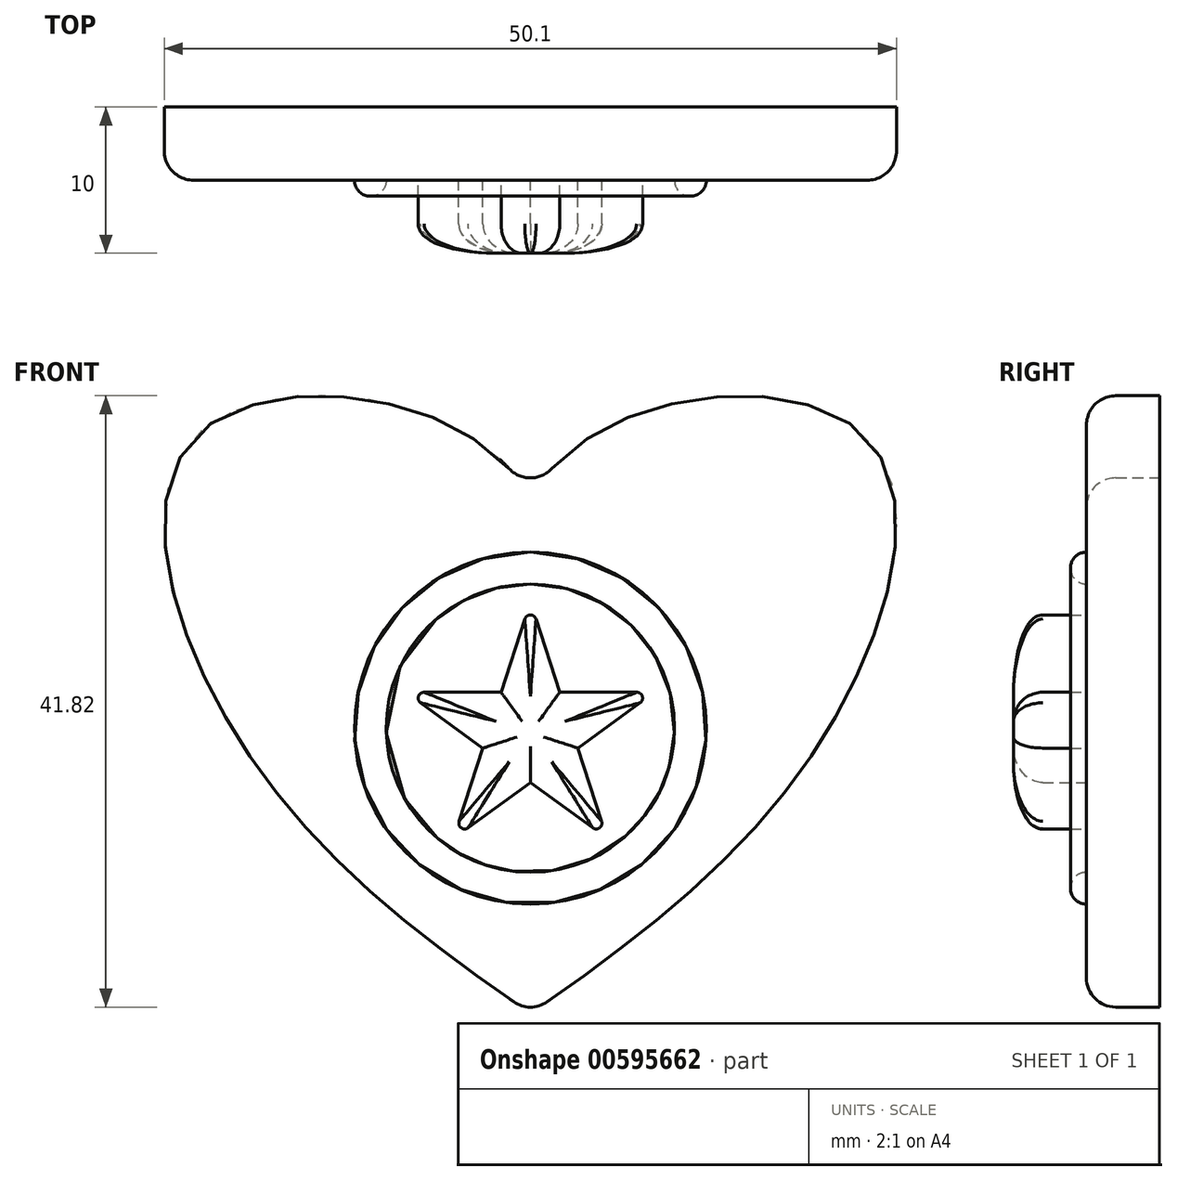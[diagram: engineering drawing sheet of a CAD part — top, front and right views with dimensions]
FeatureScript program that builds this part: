
annotation { "Feature Type Name" : "Feature", "Feature Type Description" : "" }
export const myFeature = defineFeature(function(context is Context, id is Id, definition is map)
    precondition{}
    {
        {
            var Q0;
            Q0=qCreatedBy(makeId("Front.planeOp"),FACE);
            var sketch = newSketch(context, id + "F0", { "sketchPlane" : qUnion([Q0])});
            skFitSpline(sketch, "E0", {"points": [v(0, 4.74) * mm, v(-22.34, 9.53) * mm, v(-20.92, -10.1) * mm, v(0, -30.47) * mm], "startDerivative": vector(-35.89, 67.68) * mm, "endDerivative": vector(70.46, -48.53) * mm});
            skFitSpline(sketch, "E1.MirrorCS", {"points": [v(0, 4.74) * mm, v(22.34, 9.53) * mm, v(20.92, -10.1) * mm, v(0, -30.47) * mm], "startDerivative": vector(35.89, 67.68) * mm, "endDerivative": vector(-70.46, -48.53) * mm});
            skPoint(sketch, "E2", {"position": v(-25, 1.75) * mm});
            skPoint(sketch, "E3", {"position": v(25, 1.75) * mm});
            skSolve(sketch);
        }
        {
            var Q0;
            Q0=makeQuery(id+"F0.imprint","IMPRINT",FACE,{"disambiguationData":[TD([[makeQuery(id+"F0.imprint","IMPRINT",EDGE,{"derivedFrom":sQuery(id+"F0.wireOp",EDGE,"E0")}),1.0]])]});
            extrude(context, id + "F1", {"entities" : qUnion([Q0]), "depth" : 5 * mm, "offsetDistance" : 25 * mm});
        }
        {
            var Q0;
            Q0=makeQuery(id+"F1.opExtrude","CAP_FACE",FACE,{"disambiguationData":[OSD([sQuery(id+"F0.wireOp",EDGE,"E0"),sQuery(id+"F0.wireOp",EDGE,"E1.MirrorCS")])],"isStart":false});
            var sketch = newSketch(context, id + "F2", { "sketchPlane" : qUnion([Q0])});
            skLineSegment(sketch, "E4", {"start": v(-0.38, -3.48) * mm, "end": v(-2, -8.5) * mm});
            skLineSegment(sketch, "E5", {"start": v(-2, -8.5) * mm, "end": v(-7.28, -8.5) * mm});
            skLineSegment(sketch, "E6", {"start": v(-7.51, -9.21) * mm, "end": v(-3.25, -12.31) * mm});
            skLineSegment(sketch, "E7", {"start": v(-3.25, -12.31) * mm, "end": v(-4.88, -17.32) * mm});
            skLineSegment(sketch, "E8", {"start": v(-4.26, -17.77) * mm, "end": v(0, -14.67) * mm});
            skLineSegment(sketch, "E9.MirrorCS", {"start": v(0.38, -3.48) * mm, "end": v(2, -8.5) * mm});
            skLineSegment(sketch, "E10.MirrorCS", {"start": v(2, -8.5) * mm, "end": v(7.28, -8.5) * mm});
            skLineSegment(sketch, "E11.MirrorCS", {"start": v(7.51, -9.21) * mm, "end": v(3.25, -12.31) * mm});
            skLineSegment(sketch, "E12.MirrorCS", {"start": v(3.25, -12.31) * mm, "end": v(4.88, -17.32) * mm});
            skLineSegment(sketch, "E13.MirrorCS", {"start": v(4.26, -17.77) * mm, "end": v(0, -14.67) * mm});
            skPoint(sketch, "E14.visualSharp", {"position": v(5.26, -18.5) * mm});
            skArc(sketch, "E14.filletArc", {"start": v(4.26, -17.77) * mm, "mid": v(4.73, -17.77) * mm, "end": v(4.88, -17.32) * mm});
            skPoint(sketch, "E15.visualSharp", {"position": v(8.5, -8.5) * mm});
            skArc(sketch, "E15.filletArc", {"start": v(7.51, -9.21) * mm, "mid": v(7.66, -8.77) * mm, "end": v(7.28, -8.5) * mm});
            skPoint(sketch, "E16.visualSharp", {"position": v(0, -2.3) * mm});
            skArc(sketch, "E16.filletArc", {"start": v(0.38, -3.48) * mm, "mid": v(0, -3.2) * mm, "end": v(-0.38, -3.48) * mm});
            skPoint(sketch, "E17.visualSharp", {"position": v(-8.5, -8.5) * mm});
            skArc(sketch, "E17.filletArc", {"start": v(-7.28, -8.5) * mm, "mid": v(-7.66, -8.77) * mm, "end": v(-7.51, -9.21) * mm});
            skPoint(sketch, "E18.visualSharp", {"position": v(-5.26, -18.5) * mm});
            skArc(sketch, "E18.filletArc", {"start": v(-4.88, -17.32) * mm, "mid": v(-4.73, -17.77) * mm, "end": v(-4.26, -17.77) * mm});
            skSolve(sketch);
        }
        {
            var Q0;
            Q0=makeQuery(id+"F2.imprint","IMPRINT",FACE,{"disambiguationData":[TD([[makeQuery(id+"F2.imprint","IMPRINT",EDGE,{"derivedFrom":sQuery(id+"F2.wireOp",EDGE,"E4")}),1.0]])]});
            extrude(context, id + "F3", {"entities" : qUnion([Q0]), "operationType" : NewBodyOperationType.ADD, "depth" : 5 * mm, "offsetDistance" : 25 * mm});
        }
        {
            var Q0;
            Q0=qCreatedBy(makeId("Right.planeOp"),FACE);
            var sketch = newSketch(context, id + "F4", { "sketchPlane" : qUnion([Q0])});
            skArc(sketch, "E19", {"start": v(-5, 1.09) * mm, "mid": v(-6.1, 0) * mm, "end": v(-5, -1.09) * mm});
            skLineSegment(sketch, "E20", {"start": v(-5, 1.09) * mm, "end": v(-5, -1.09) * mm});
            skSolve(sketch);
        }
        {
            var Q0;
            Q0=makeQuery(id+"F1.opExtrude","CAP_FACE",FACE,{"disambiguationData":[OSD([sQuery(id+"F0.wireOp",EDGE,"E0"),sQuery(id+"F0.wireOp",EDGE,"E1.MirrorCS")])],"isStart":false});
            var sketch = newSketch(context, id + "F5", { "sketchPlane" : qUnion([Q0])});
            skCircle(sketch, "E21", {"center": v(0, -10.95) * mm, "radius": 10.95 * mm});
            skSolve(sketch);
        }
        {
            var Q0;
            Q0=makeQuery(id+"F4.imprint","IMPRINT",FACE,{"disambiguationData":[TD([[makeQuery(id+"F4.imprint","IMPRINT",EDGE,{"derivedFrom":sQuery(id+"F4.wireOp",EDGE,"E19")}),1.0]])]});
            var Q1;
            Q1=sQuery(id+"F5.wireOp",EDGE,"E21");
            sweep(context, id + "F6", {"profiles" : qUnion([Q0]), "path" : qUnion([Q1])});
        }
        {
            var Q0;
            Q0=makeQuery(id+"F3.opExtrude","CAP_FACE",FACE,{"disambiguationData":[OSD([sQuery(id+"F2.wireOp",EDGE,"E4"),sQuery(id+"F2.wireOp",EDGE,"E5"),sQuery(id+"F2.wireOp",EDGE,"E6"),sQuery(id+"F2.wireOp",EDGE,"E7"),sQuery(id+"F2.wireOp",EDGE,"E8"),sQuery(id+"F2.wireOp",EDGE,"E9.MirrorCS"),sQuery(id+"F2.wireOp",EDGE,"E10.MirrorCS"),sQuery(id+"F2.wireOp",EDGE,"E11.MirrorCS"),sQuery(id+"F2.wireOp",EDGE,"E12.MirrorCS"),sQuery(id+"F2.wireOp",EDGE,"E13.MirrorCS"),sQuery(id+"F2.wireOp",EDGE,"E14.filletArc"),sQuery(id+"F2.wireOp",EDGE,"E15.filletArc"),sQuery(id+"F2.wireOp",EDGE,"E16.filletArc"),sQuery(id+"F2.wireOp",EDGE,"E17.filletArc"),sQuery(id+"F2.wireOp",EDGE,"E18.filletArc")])],"isStart":false});
            var Q1;
            Q1=makeQuery(id+"F1.opExtrude","CAP_EDGE",EDGE,{"disambiguationData":[OSD([sQuery(id+"F0.wireOp",EDGE,"E0")])],"isStart":false});
            var Q2;
            Q2=makeQuery(id+"F1.opExtrude","CAP_EDGE",EDGE,{"disambiguationData":[OSD([sQuery(id+"F0.wireOp",EDGE,"E1.MirrorCS")])],"isStart":false});
            var Q3;
            {var subQ0=sQuery(id+"F0.wireOp",EDGE,"E1.MirrorCS");var subQ1=sQuery(id+"F0.wireOp",EDGE,"E0");Q3=makeQuery(id+"F1.opExtrude","SWEPT_EDGE",EDGE,{"disambiguationData":[OSD([subQ1,subQ0]),TDD([makeQuery(id+"F0.imprint","INTERSECT",VERTEX,{"disambiguationData":[OD(1.0)],"derivedFrom":[subQ1,subQ0]})])]});}
            var Q4;
            {var subQ0=sQuery(id+"F0.wireOp",EDGE,"E1.MirrorCS");var subQ1=sQuery(id+"F0.wireOp",EDGE,"E0");Q4=makeQuery(id+"F1.opExtrude","SWEPT_EDGE",EDGE,{"disambiguationData":[OSD([subQ1,subQ0]),TDD([makeQuery(id+"F0.imprint","INTERSECT",VERTEX,{"disambiguationData":[OD(0.0)],"derivedFrom":[subQ1,subQ0]})])]});}
            fillet(context, id + "F7", {"entities" : qUnion([Q0, Q1, Q2, Q3, Q4]), "radius" : 2 * mm, "tangentPropagation" : true, "allowEdgeOverflow" : false});
        }
    });
